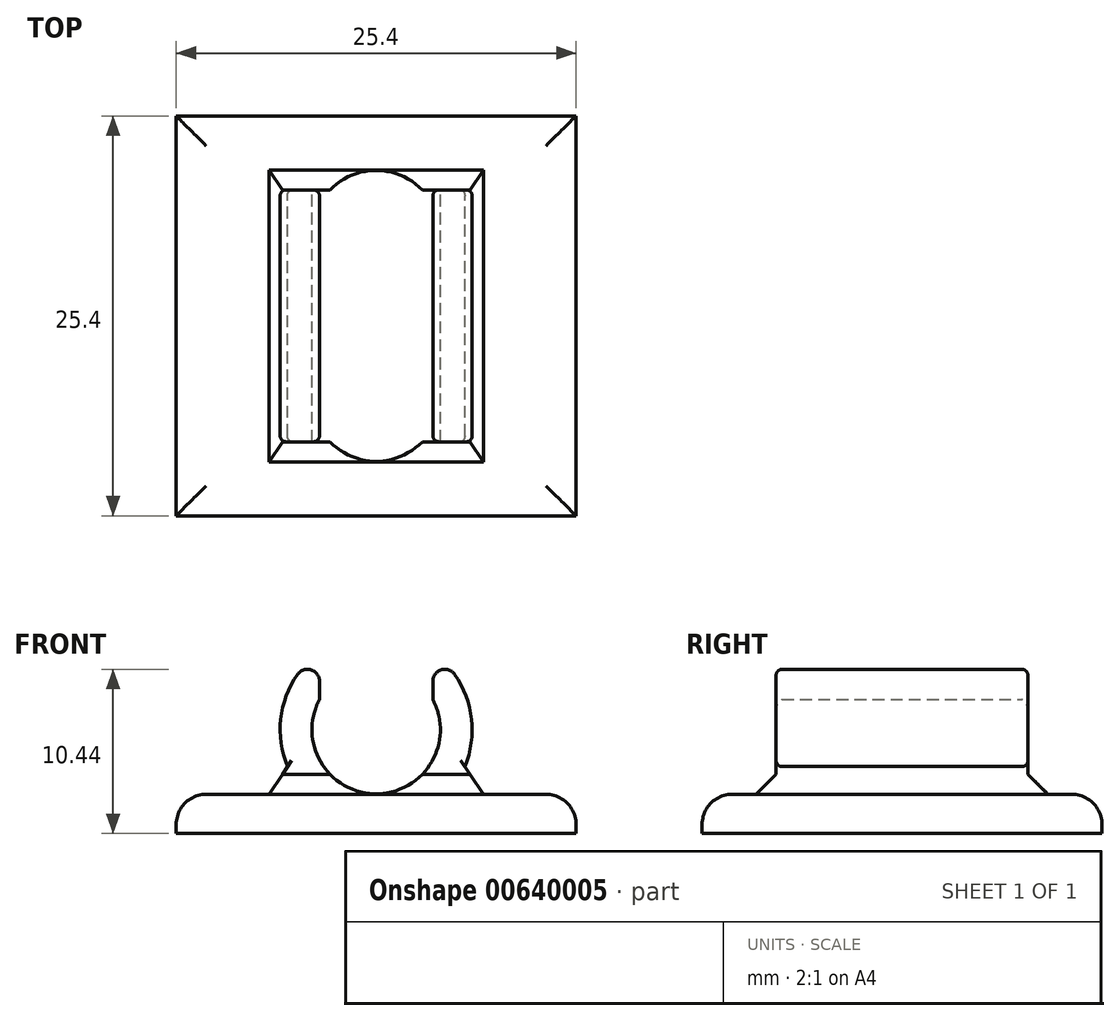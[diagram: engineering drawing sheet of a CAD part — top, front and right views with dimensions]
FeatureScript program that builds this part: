
annotation { "Feature Type Name" : "Feature", "Feature Type Description" : "" }
export const myFeature = defineFeature(function(context is Context, id is Id, definition is map)
    precondition{}
    {
        {
            var Q0;
            Q0=qCreatedBy(makeId("Top.planeOp"),FACE);
            var sketch = newSketch(context, id + "F0", { "sketchPlane" : qUnion([Q0])});
            skLineSegment(sketch, "E0.bottom", {"start": v(-12.7, 12.7) * mm, "end": v(12.7, 12.7) * mm});
            skLineSegment(sketch, "E0.top", {"start": v(-12.7, -12.7) * mm, "end": v(12.7, -12.7) * mm});
            skLineSegment(sketch, "E0.left", {"start": v(-12.7, 12.7) * mm, "end": v(-12.7, -12.7) * mm});
            skLineSegment(sketch, "E0.right", {"start": v(12.7, 12.7) * mm, "end": v(12.7, -12.7) * mm});
            skSolve(sketch);
        }
        {
            var Q0;
            Q0 = qSketchRegion(id + "F0", true);
            extrude(context, id + "F1", {"entities" : qUnion([Q0]), "depth" : 2.5 * mm, "offsetDistance" : 25.4 * mm});
        }
        {
            var Q0;
            Q0=makeQuery(id+"F1.opExtrude","CAP_EDGE",EDGE,{"disambiguationData":[OSD([sQuery(id+"F0.wireOp",EDGE,"E0.top")])],"isStart":false});
            var Q1;
            Q1=makeQuery(id+"F1.opExtrude","CAP_EDGE",EDGE,{"disambiguationData":[OSD([sQuery(id+"F0.wireOp",EDGE,"E0.left")])],"isStart":false});
            var Q2;
            Q2=makeQuery(id+"F1.opExtrude","CAP_EDGE",EDGE,{"disambiguationData":[OSD([sQuery(id+"F0.wireOp",EDGE,"E0.bottom")])],"isStart":false});
            var Q3;
            Q3=makeQuery(id+"F1.opExtrude","CAP_EDGE",EDGE,{"disambiguationData":[OSD([sQuery(id+"F0.wireOp",EDGE,"E0.right")])],"isStart":false});
            fillet(context, id + "F2", {"entities" : qUnion([Q0, Q1, Q2, Q3]), "radius" : 1.9 * mm, "tangentPropagation" : true, "allowEdgeOverflow" : false});
        }
        {
            var Q0;
            Q0=qCreatedBy(makeId("Front.planeOp"),FACE);
            var sketch = newSketch(context, id + "F3", { "sketchPlane" : qUnion([Q0])});
            skPoint(sketch, "E1.0", {"position": v(0, 2.5) * mm});
            skLineSegment(sketch, "E2.0", {"start": v(-10.8, 2.5) * mm, "end": v(-4.51, 2.5) * mm});
            skArc(sketch, "E3", {"start": v(-3.6, 8.5) * mm, "mid": v(0, 2.52) * mm, "end": v(3.6, 8.5) * mm});
            skLineSegment(sketch, "E4.0.0", {"start": v(12.7, 0) * mm, "end": v(12.7, 0.6) * mm});
            skLineSegment(sketch, "E4.0.1", {"start": v(12.7, 0.6) * mm, "end": v(-12.7, 0.6) * mm});
            skLineSegment(sketch, "E4.0.2", {"start": v(-12.7, 0.6) * mm, "end": v(-12.7, 0) * mm});
            skLineSegment(sketch, "E4.0.3", {"start": v(-12.7, 0) * mm, "end": v(12.7, 0) * mm});
            skArc(sketch, "E5.trimOffspring", {"start": v(1.06, 0.6) * mm, "mid": v(5.64, 4.28) * mm, "end": v(4.98, 10.11) * mm});
            skLineSegment(sketch, "E6", {"start": v(3.6, 9.67) * mm, "end": v(3.6, 8.5) * mm});
            skLineSegment(sketch, "E7", {"start": v(-3.6, 9.67) * mm, "end": v(-3.6, 8.5) * mm});
            skLineSegment(sketch, "E8.trimOffspring", {"start": v(4.51, 2.5) * mm, "end": v(10.8, 2.5) * mm});
            skArc(sketch, "E9.trimOffspring", {"start": v(-4.98, 10.11) * mm, "mid": v(-5.64, 4.28) * mm, "end": v(-1.06, 0.6) * mm});
            skPoint(sketch, "E10.visualSharp", {"position": v(-3.6, 11.52) * mm});
            skArc(sketch, "E10.filletArc", {"start": v(-3.6, 9.67) * mm, "mid": v(-4.13, 10.4) * mm, "end": v(-4.98, 10.11) * mm});
            skPoint(sketch, "E11.visualSharp", {"position": v(3.6, 11.52) * mm});
            skArc(sketch, "E11.filletArc", {"start": v(4.98, 10.11) * mm, "mid": v(4.13, 10.4) * mm, "end": v(3.6, 9.67) * mm});
            skSolve(sketch);
        }
        {
            var Q0;
            Q0 = qSketchRegion(id + "F3", true);
            extrude(context, id + "F4", {"entities" : qUnion([Q0]), "operationType" : NewBodyOperationType.ADD, "endBound" : BoundingType.SYMMETRIC, "depth" : 16 * mm, "offsetDistance" : 25.4 * mm});
        }
        {
            var Q0;
            Q0=makeQuery(id+"F4.boolean.opBoolean","INTERSECT",EDGE,{"derivedFrom":[makeQuery(id+"F1.opExtrude","CAP_FACE",FACE,{"disambiguationData":[OSD([sQuery(id+"F0.wireOp",EDGE,"E0.bottom"),sQuery(id+"F0.wireOp",EDGE,"E0.top"),sQuery(id+"F0.wireOp",EDGE,"E0.left"),sQuery(id+"F0.wireOp",EDGE,"E0.right")])],"isStart":false}),makeQuery(id+"F4.opExtrude","SWEPT_FACE",FACE,{"disambiguationData":[OSD([sQuery(id+"F3.wireOp",EDGE,"E9.trimOffspring")])]})]});
            var Q1;
            Q1=makeQuery(id+"F4.boolean.opBoolean","INTERSECT",EDGE,{"derivedFrom":[makeQuery(id+"F1.opExtrude","CAP_FACE",FACE,{"disambiguationData":[OSD([sQuery(id+"F0.wireOp",EDGE,"E0.bottom"),sQuery(id+"F0.wireOp",EDGE,"E0.top"),sQuery(id+"F0.wireOp",EDGE,"E0.left"),sQuery(id+"F0.wireOp",EDGE,"E0.right")])],"isStart":false}),makeQuery(id+"F4.opExtrude","CAP_FACE",FACE,{"disambiguationData":[OSD([sQuery(id+"F3.wireOp",EDGE,"E3"),sQuery(id+"F3.wireOp",EDGE,"E4.0.0"),sQuery(id+"F3.wireOp",EDGE,"E4.0.1"),sQuery(id+"F3.wireOp",EDGE,"E4.0.2"),sQuery(id+"F3.wireOp",EDGE,"E4.0.3"),sQuery(id+"F3.wireOp",EDGE,"E5.trimOffspring"),sQuery(id+"F3.wireOp",EDGE,"E6"),sQuery(id+"F3.wireOp",EDGE,"E7"),sQuery(id+"F3.wireOp",EDGE,"E9.trimOffspring"),sQuery(id+"F3.wireOp",EDGE,"E10.filletArc"),sQuery(id+"F3.wireOp",EDGE,"E11.filletArc")])],"isStart":false})]});
            var Q2;
            Q2=makeQuery(id+"F4.boolean.opBoolean","INTERSECT",EDGE,{"derivedFrom":[makeQuery(id+"F1.opExtrude","CAP_FACE",FACE,{"disambiguationData":[OSD([sQuery(id+"F0.wireOp",EDGE,"E0.bottom"),sQuery(id+"F0.wireOp",EDGE,"E0.top"),sQuery(id+"F0.wireOp",EDGE,"E0.left"),sQuery(id+"F0.wireOp",EDGE,"E0.right")])],"isStart":false}),makeQuery(id+"F4.opExtrude","CAP_FACE",FACE,{"disambiguationData":[OSD([sQuery(id+"F3.wireOp",EDGE,"E3"),sQuery(id+"F3.wireOp",EDGE,"E4.0.0"),sQuery(id+"F3.wireOp",EDGE,"E4.0.1"),sQuery(id+"F3.wireOp",EDGE,"E4.0.2"),sQuery(id+"F3.wireOp",EDGE,"E4.0.3"),sQuery(id+"F3.wireOp",EDGE,"E5.trimOffspring"),sQuery(id+"F3.wireOp",EDGE,"E6"),sQuery(id+"F3.wireOp",EDGE,"E7"),sQuery(id+"F3.wireOp",EDGE,"E9.trimOffspring"),sQuery(id+"F3.wireOp",EDGE,"E10.filletArc"),sQuery(id+"F3.wireOp",EDGE,"E11.filletArc")])],"isStart":true})]});
            var Q3;
            Q3=makeQuery(id+"F4.boolean.opBoolean","INTERSECT",EDGE,{"derivedFrom":[makeQuery(id+"F1.opExtrude","CAP_FACE",FACE,{"disambiguationData":[OSD([sQuery(id+"F0.wireOp",EDGE,"E0.bottom"),sQuery(id+"F0.wireOp",EDGE,"E0.top"),sQuery(id+"F0.wireOp",EDGE,"E0.left"),sQuery(id+"F0.wireOp",EDGE,"E0.right")])],"isStart":false}),makeQuery(id+"F4.opExtrude","SWEPT_FACE",FACE,{"disambiguationData":[OSD([sQuery(id+"F3.wireOp",EDGE,"E5.trimOffspring")])]})]});
            chamfer(context, id + "F5", {"entities" : qUnion([Q0, Q1, Q2, Q3]), "width" : 1.27 * mm, "tangentPropagation" : true});
        }
        {
            var Q0;
            Q0=makeQuery(id+"F4.opExtrude","CAP_EDGE",EDGE,{"disambiguationData":[OSD([sQuery(id+"F3.wireOp",EDGE,"E10.filletArc")])],"isStart":false});
            var Q1;
            Q1=makeQuery(id+"F4.opExtrude","CAP_EDGE",EDGE,{"disambiguationData":[OSD([sQuery(id+"F3.wireOp",EDGE,"E9.trimOffspring")])],"isStart":false});
            var Q2;
            Q2=makeQuery(id+"F4.opExtrude","CAP_EDGE",EDGE,{"disambiguationData":[OSD([sQuery(id+"F3.wireOp",EDGE,"E11.filletArc")])],"isStart":false});
            var Q3;
            Q3=makeQuery(id+"F4.opExtrude","CAP_EDGE",EDGE,{"disambiguationData":[OSD([sQuery(id+"F3.wireOp",EDGE,"E5.trimOffspring")])],"isStart":false});
            var Q4;
            Q4=makeQuery(id+"F4.opExtrude","CAP_EDGE",EDGE,{"disambiguationData":[OSD([sQuery(id+"F3.wireOp",EDGE,"E9.trimOffspring")])],"isStart":true});
            var Q5;
            Q5=makeQuery(id+"F4.opExtrude","CAP_EDGE",EDGE,{"disambiguationData":[OSD([sQuery(id+"F3.wireOp",EDGE,"E5.trimOffspring")])],"isStart":true});
            fillet(context, id + "F6", {"entities" : qUnion([Q0, Q1, Q2, Q3, Q4, Q5]), "radius" : 0.38 * mm, "tangentPropagation" : true, "allowEdgeOverflow" : false});
        }
    });
